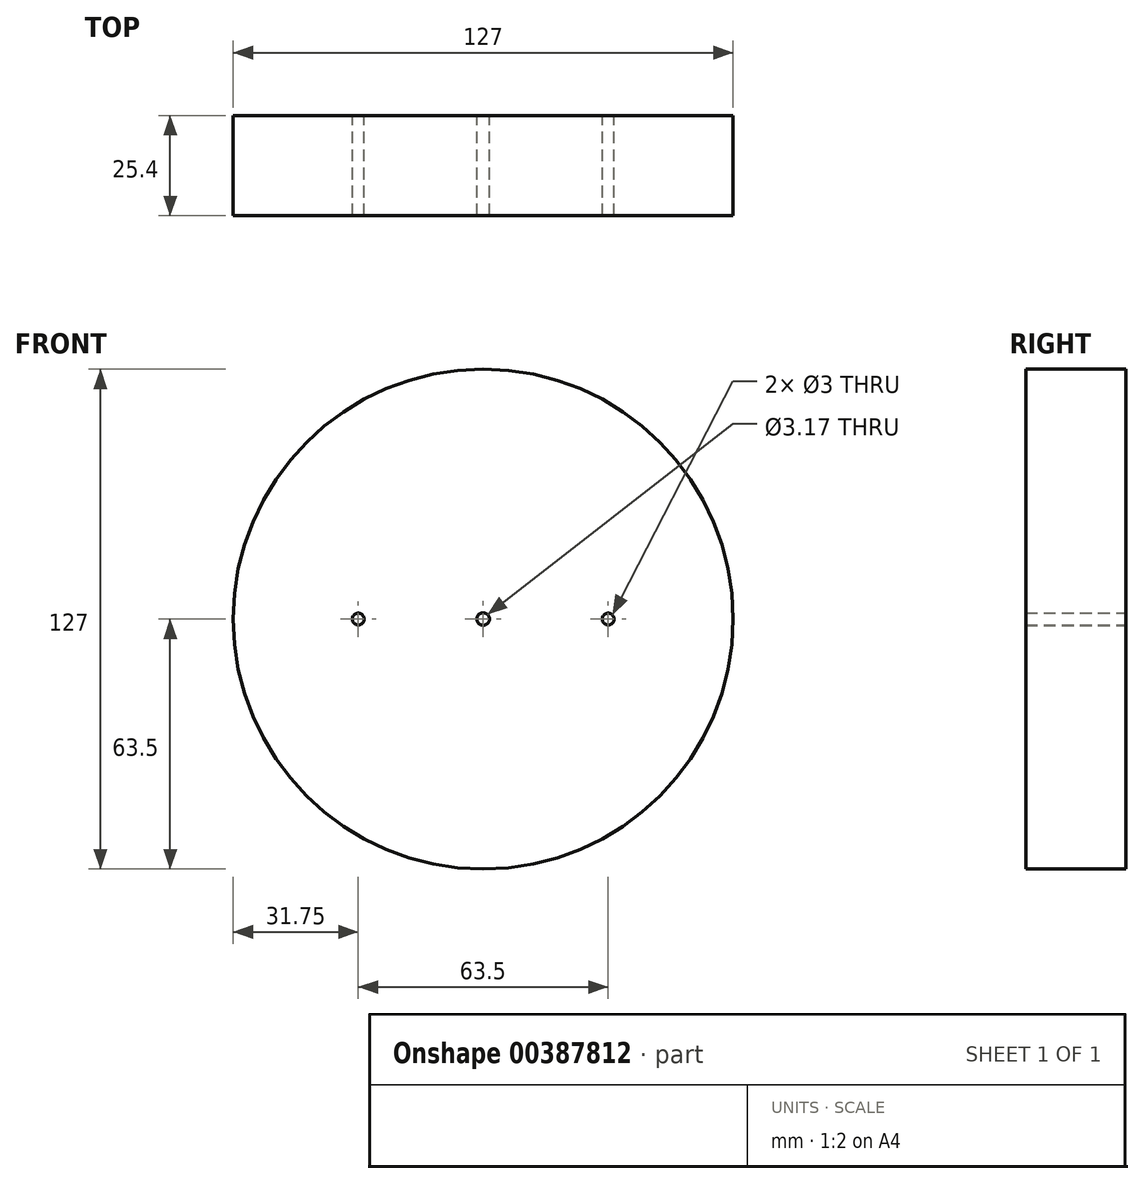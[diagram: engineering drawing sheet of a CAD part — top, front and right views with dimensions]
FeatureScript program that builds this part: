
annotation { "Feature Type Name" : "Feature", "Feature Type Description" : "" }
export const myFeature = defineFeature(function(context is Context, id is Id, definition is map)
    precondition{}
    {
        {
            var Q0;
            Q0=qCreatedBy(makeId("Front.planeOp"),FACE);
            var sketch = newSketch(context, id + "F0", { "sketchPlane" : qUnion([Q0])});
            skCircle(sketch, "E0", {"center": v(0, 0) * mm, "radius": 63.5 * mm});
            skCircle(sketch, "E1", {"center": v(0, 0) * mm, "radius": 1.59 * mm});
            skLineSegment(sketch, "E2", {"start": v(0, 0) * mm, "end": v(-63.5, 0) * mm});
            skLineSegment(sketch, "E3", {"start": v(0, 0) * mm, "end": v(63.5, 0) * mm});
            skCircle(sketch, "E4", {"center": v(-31.75, 0) * mm, "radius": 1.5 * mm});
            skCircle(sketch, "E5", {"center": v(31.75, 0) * mm, "radius": 1.5 * mm});
            skSolve(sketch);
        }
        {
            var Q0;
            Q0=makeQuery(id+"F0.imprint","IMPRINT",FACE,{"disambiguationData":[TD([[makeQuery(id+"F0.imprint","IMPRINT",EDGE,{"derivedFrom":sQuery(id+"F0.wireOp",EDGE,"E0")}),1.0]])]});
            extrude(context, id + "F1", {"entities" : qUnion([Q0]), "depth" : 25.4 * mm, "offsetDistance" : 25.4 * mm});
        }
    });
